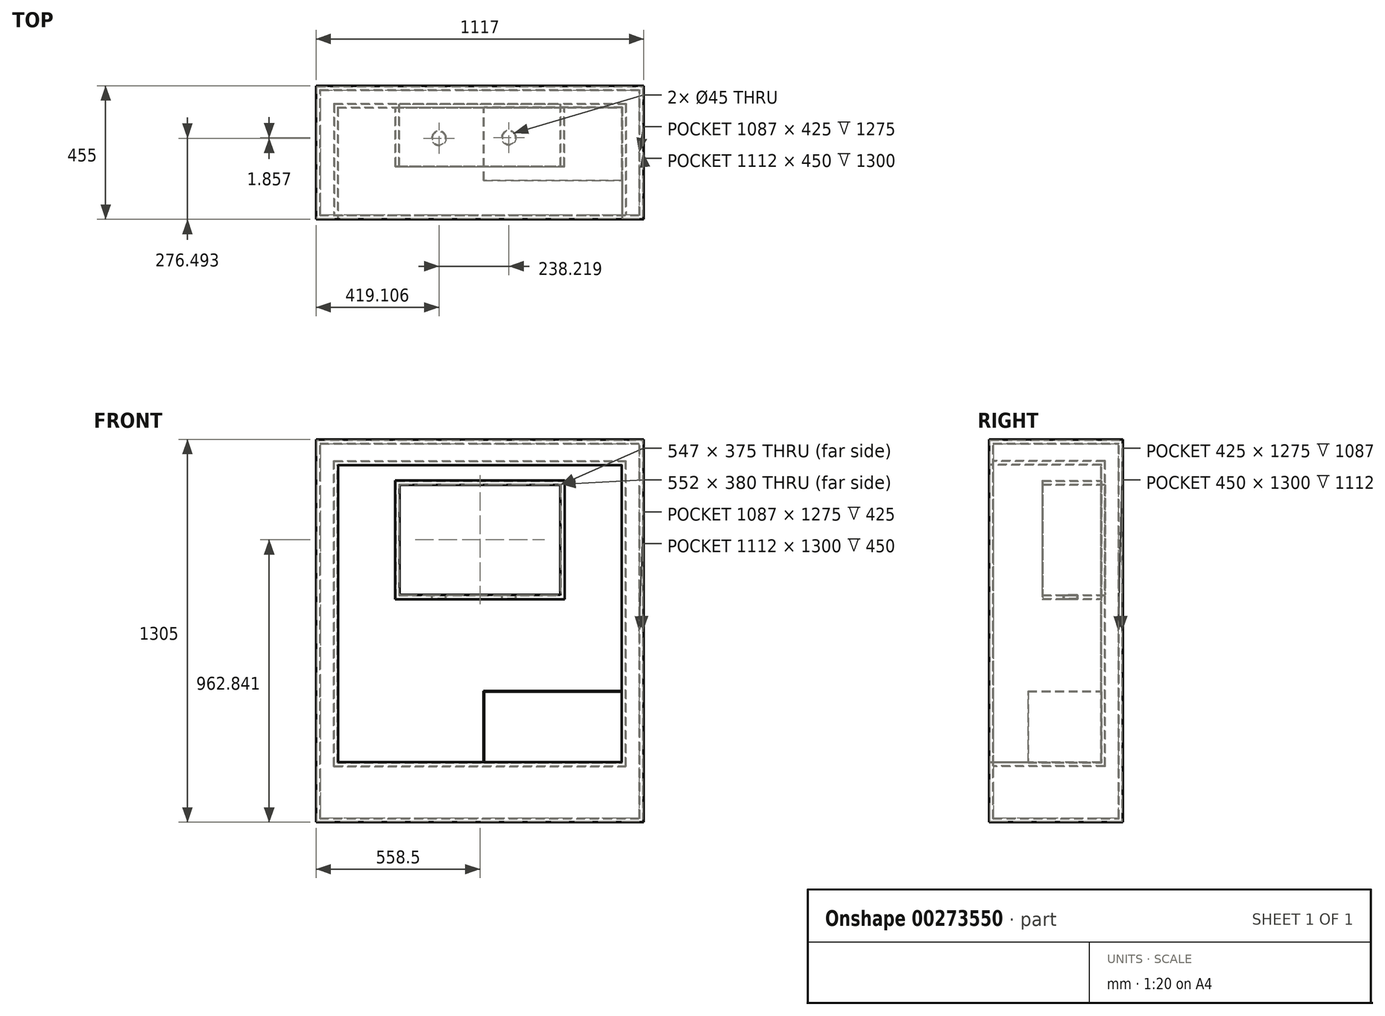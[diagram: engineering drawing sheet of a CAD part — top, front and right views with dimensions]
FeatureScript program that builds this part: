
annotation { "Feature Type Name" : "Feature", "Feature Type Description" : "" }
export const myFeature = defineFeature(function(context is Context, id is Id, definition is map)
    precondition{}
    {
        {
            var Q0;
            Q0=qCreatedBy(makeId("Top.planeOp"),FACE);
            var sketch = newSketch(context, id + "F0", { "sketchPlane" : qUnion([Q0])});
            skLineSegment(sketch, "E0.bottom", {"start": v(-556, -225) * mm, "end": v(556, -225) * mm});
            skLineSegment(sketch, "E0.top", {"start": v(-556, 225) * mm, "end": v(556, 225) * mm});
            skLineSegment(sketch, "E0.left", {"start": v(-556, -225) * mm, "end": v(-556, 225) * mm});
            skLineSegment(sketch, "E0.right", {"start": v(556, -225) * mm, "end": v(556, 225) * mm});
            skPoint(sketch, "E0.middle", {"position": v(0, 0) * mm});
            skSolve(sketch);
        }
        {
            var Q0;
            Q0=qSketchRegion(id+"F0",true);
            extrude(context, id + "F1", {"entities" : qUnion([Q0]), "oppositeDirection" : true, "depth" : 1300 * mm});
        }
        {
            var Q0;
            Q0=makeQuery(id+"F1.opExtrude","SWEPT_FACE",FACE,{"disambiguationData":[OSD([sQuery(id+"F0.wireOp",EDGE,"E0.bottom")])]});
            var sketch = newSketch(context, id + "F2", { "sketchPlane" : qUnion([Q0])});
            skLineSegment(sketch, "E1.bottom", {"start": v(-486, -1100) * mm, "end": v(486, -1100) * mm});
            skLineSegment(sketch, "E1.top", {"start": v(-486, -82.5) * mm, "end": v(486, -82.5) * mm});
            skLineSegment(sketch, "E1.left", {"start": v(-486, -1100) * mm, "end": v(-486, -82.5) * mm});
            skLineSegment(sketch, "E1.right", {"start": v(486, -1100) * mm, "end": v(486, -82.5) * mm});
            skPoint(sketch, "E1.middle", {"position": v(0, -591.25) * mm});
            skSolve(sketch);
        }
        {
            var Q0;
            Q0=makeQuery(id+"F2.imprint","IMPRINT",FACE,{"disambiguationData":[TD([[makeQuery(id+"F2.imprint","IMPRINT",EDGE,{"derivedFrom":sQuery(id+"F2.wireOp",EDGE,"E1.bottom")}),1.0]])]});
            extrude(context, id + "F3", {"entities" : qUnion([Q0]), "operationType" : NewBodyOperationType.REMOVE, "oppositeDirection" : true, "depth" : 380 * mm});
        }
        {
            var Q0;
            {var subQ0=sQuery(id+"F2.wireOp",EDGE,"E1.top");var subQ1=sQuery(id+"F2.wireOp",EDGE,"E1.left");var subQ2=sQuery(id+"F2.wireOp",EDGE,"E1.right");Q0=makeQuery(id+"FC6qhIdo42RC5vu_1.boolean.opBoolean","SPLIT",FACE,{"disambiguationData":[TD([makeQuery(id+"F3.boolean.opBoolean","COPY",FACE,{"derivedFrom":makeQuery(id+"F3.opExtrude","SWEPT_FACE",FACE,{"disambiguationData":[OSD([subQ0])]})})])],"derivedFrom":makeQuery(id+"F3.boolean.opBoolean","COPY",FACE,{"derivedFrom":makeQuery(id+"F3.opExtrude","CAP_FACE",FACE,{"disambiguationData":[OSD([sQuery(id+"F2.wireOp",EDGE,"E1.bottom"),subQ0,subQ1,subQ2])],"isStart":false})})});}
            var sketch = newSketch(context, id + "F4", { "sketchPlane" : qUnion([Q0])});
            skLineSegment(sketch, "E2.bottom", {"start": v(-286, -139.66) * mm, "end": v(286, -139.66) * mm});
            skLineSegment(sketch, "E2.top", {"start": v(-286, -539.66) * mm, "end": v(286, -539.66) * mm});
            skLineSegment(sketch, "E2.left", {"start": v(-286, -139.66) * mm, "end": v(-286, -539.66) * mm});
            skLineSegment(sketch, "E2.right", {"start": v(286, -139.66) * mm, "end": v(286, -539.66) * mm});
            skSolve(sketch);
        }
        {
            var Q0;
            Q0=makeQuery(id+"F4.imprint","IMPRINT",FACE,{"disambiguationData":[TD([[makeQuery(id+"F4.imprint","IMPRINT",EDGE,{"derivedFrom":sQuery(id+"F4.wireOp",EDGE,"E2.bottom")}),-1.0]])]});
            extrude(context, id + "F5", {"entities" : qUnion([Q0]), "operationType" : NewBodyOperationType.ADD, "depth" : 200 * mm});
        }
        {
            var Q0;
            Q0=makeQuery(id+"F5.opExtrude","CAP_FACE",FACE,{"disambiguationData":[OSD([sQuery(id+"F4.wireOp",EDGE,"E2.bottom"),sQuery(id+"F4.wireOp",EDGE,"E2.top"),sQuery(id+"F4.wireOp",EDGE,"E2.left"),sQuery(id+"F4.wireOp",EDGE,"E2.right")])],"isStart":false});
            shell(context, id + "F6", {"entities" : qUnion([Q0]), "thickness" : 10 * mm});
        }
        {
            var Q0;
            Q0=makeQuery(id+"F6.opShell","OFFSET_FACE",FACE,{"disambiguationData":[OSD([sQuery(id+"F0.wireOp",EDGE,"E0.top")])]});
            var sketch = newSketch(context, id + "F7", { "sketchPlane" : qUnion([Q0])});
            skCircle(sketch, "E3", {"center": v(0, -274.2) * mm, "radius": 100 * mm});
            skSolve(sketch);
        }
        {
            var Q0;
            Q0=sQuery(id+"F7.wireOp",EDGE,"E3");
            extrude(context, id + "F8", {"bodyType" : ToolBodyType.SURFACE, "surfaceEntities" : qUnion([Q0]), "depth" : 30 * mm});
        }
        {
            var Q0;
            Q0=makeQuery(id+"F6.opShell","OFFSET_FACE",FACE,{"disambiguationData":[OSD([sQuery(id+"F4.wireOp",EDGE,"E2.top")])]});
            var sketch = newSketch(context, id + "F9", { "sketchPlane" : qUnion([Q0])});
            skCircle(sketch, "E4", {"center": v(-139.4, 49) * mm, "radius": 25 * mm});
            skCircle(sketch, "E5", {"center": v(98.82, 50.85) * mm, "radius": 25 * mm});
            skSolve(sketch);
        }
        {
            var Q0;
            Q0 = qSketchRegion(id + "F9", true);
            extrude(context, id + "F10", {"entities" : qUnion([Q0]), "operationType" : NewBodyOperationType.REMOVE, "oppositeDirection" : true, "depth" : 20 * mm});
        }
        {
            var Q0;
            Q0=makeQuery(id+"F3.boolean.opBoolean","COPY",FACE,{"derivedFrom":makeQuery(id+"F3.opExtrude","CAP_FACE",FACE,{"disambiguationData":[OSD([sQuery(id+"F2.wireOp",EDGE,"E1.bottom"),sQuery(id+"F2.wireOp",EDGE,"E1.top"),sQuery(id+"F2.wireOp",EDGE,"E1.left"),sQuery(id+"F2.wireOp",EDGE,"E1.right")])],"isStart":false})});
            var sketch = newSketch(context, id + "F11", { "sketchPlane" : qUnion([Q0])});
            skLineSegment(sketch, "E6.bottom", {"start": v(486, -857.12) * mm, "end": v(14, -857.12) * mm});
            skLineSegment(sketch, "E6.top", {"start": v(486, -1100) * mm, "end": v(14, -1100) * mm});
            skLineSegment(sketch, "E6.left", {"start": v(486, -857.12) * mm, "end": v(486, -1100) * mm});
            skLineSegment(sketch, "E6.right", {"start": v(14, -857.12) * mm, "end": v(14, -1100) * mm});
            skSolve(sketch);
        }
        {
            var Q0;
            Q0 = qSketchRegion(id + "F11", true);
            extrude(context, id + "F12", {"entities" : qUnion([Q0]), "operationType" : NewBodyOperationType.ADD, "depth" : 250 * mm});
        }
        {
            var Q0;
            Q0=makeQuery(id+"F12.opExtrude","CAP_FACE",FACE,{"disambiguationData":[OSD([sQuery(id+"F11.wireOp",EDGE,"E6.bottom"),sQuery(id+"F11.wireOp",EDGE,"E6.top"),sQuery(id+"F11.wireOp",EDGE,"E6.left"),sQuery(id+"F11.wireOp",EDGE,"E6.right")])],"isStart":false});
            shell(context, id + "F13", {"entities" : qUnion([Q0]), "thickness" : 2.5 * mm, "oppositeDirection" : true});
        }
    });
